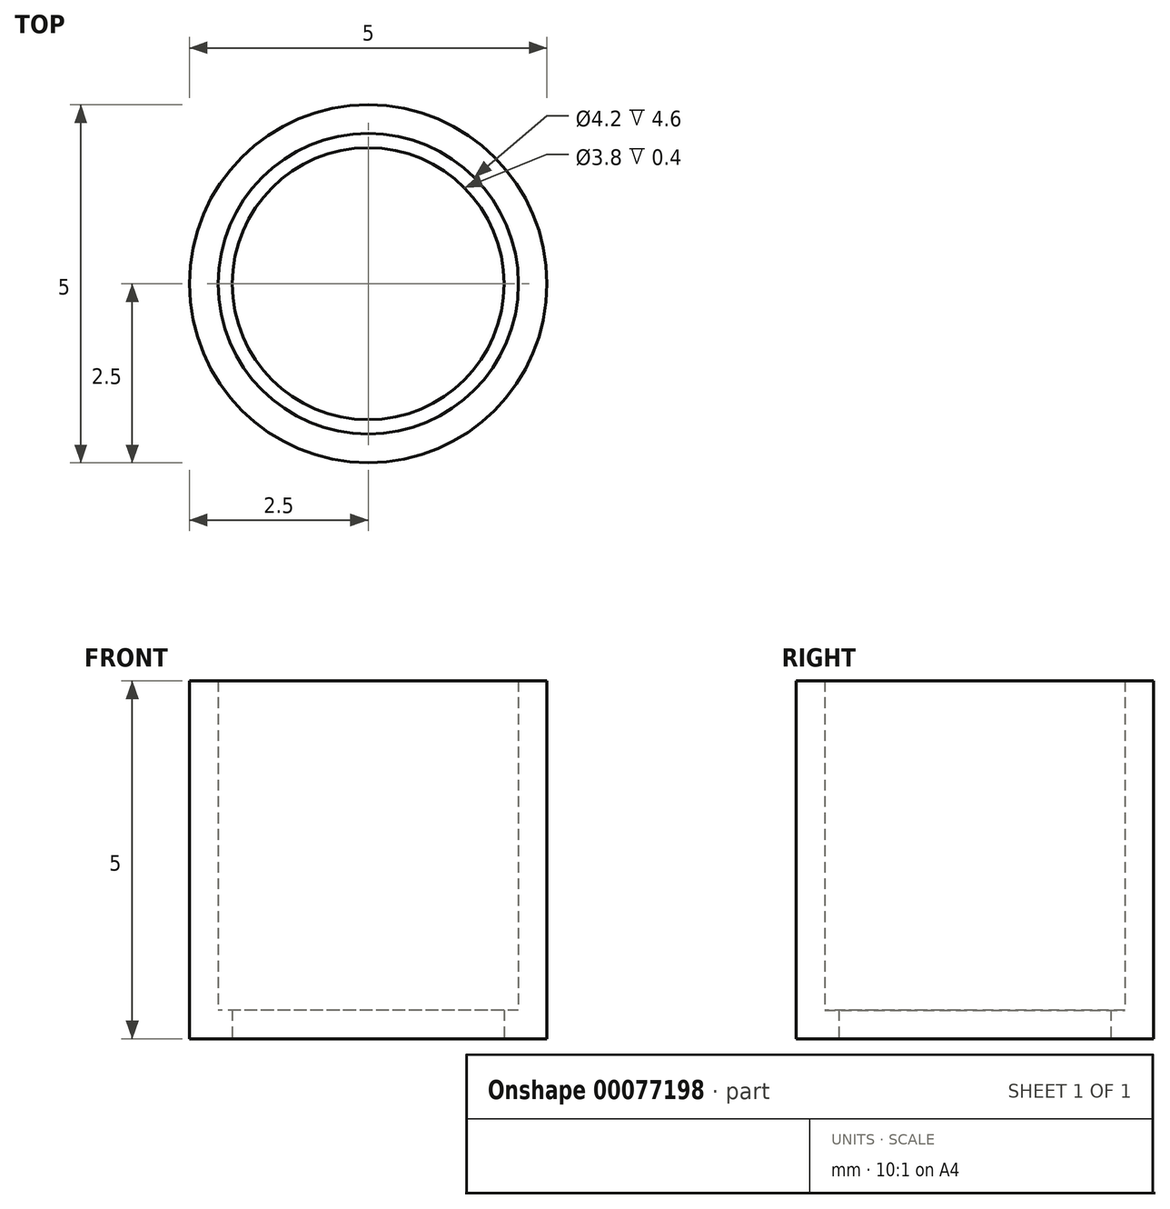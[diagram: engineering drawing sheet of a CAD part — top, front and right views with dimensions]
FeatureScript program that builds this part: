
annotation { "Feature Type Name" : "Feature", "Feature Type Description" : "" }
export const myFeature = defineFeature(function(context is Context, id is Id, definition is map)
    precondition{}
    {
        {
            var Q0;
            Q0=qCreatedBy(makeId("Top.planeOp"),FACE);
            var sketch = newSketch(context, id + "F0", { "sketchPlane" : qUnion([Q0])});
            skCircle(sketch, "E0", {"center": v(0, 0) * mm, "radius": 2.5 * mm});
            skSolve(sketch);
        }
        {
            var Q0;
            Q0=qSketchRegion(id+"F0",true);
            extrude(context, id + "F1", {"entities" : qUnion([Q0]), "depth" : 5 * mm});
        }
        {
            var Q0;
            Q0=makeQuery(id+"F1.opExtrude","CAP_FACE",FACE,{"disambiguationData":[OSD([sQuery(id+"F0.wireOp",EDGE,"E0")])],"isStart":false});
            shell(context, id + "F2", {"entities" : qUnion([Q0]), "thickness" : .4 * mm});
        }
        {
            var Q0;
            Q0=makeQuery(id+"F1.opExtrude","CAP_FACE",FACE,{"disambiguationData":[OSD([sQuery(id+"F0.wireOp",EDGE,"E0")])],"isStart":true});
            var sketch = newSketch(context, id + "F3", { "sketchPlane" : qUnion([Q0])});
            skCircle(sketch, "E1", {"center": v(0, 0) * mm, "radius": 1.9 * mm});
            skSolve(sketch);
        }
        {
            var Q0;
            Q0=qSketchRegion(id+"F3",true);
            extrude(context, id + "F4", {"entities" : qUnion([Q0]), "operationType" : NewBodyOperationType.REMOVE, "oppositeDirection" : true, "depth" : 25 * mm});
        }
    });
